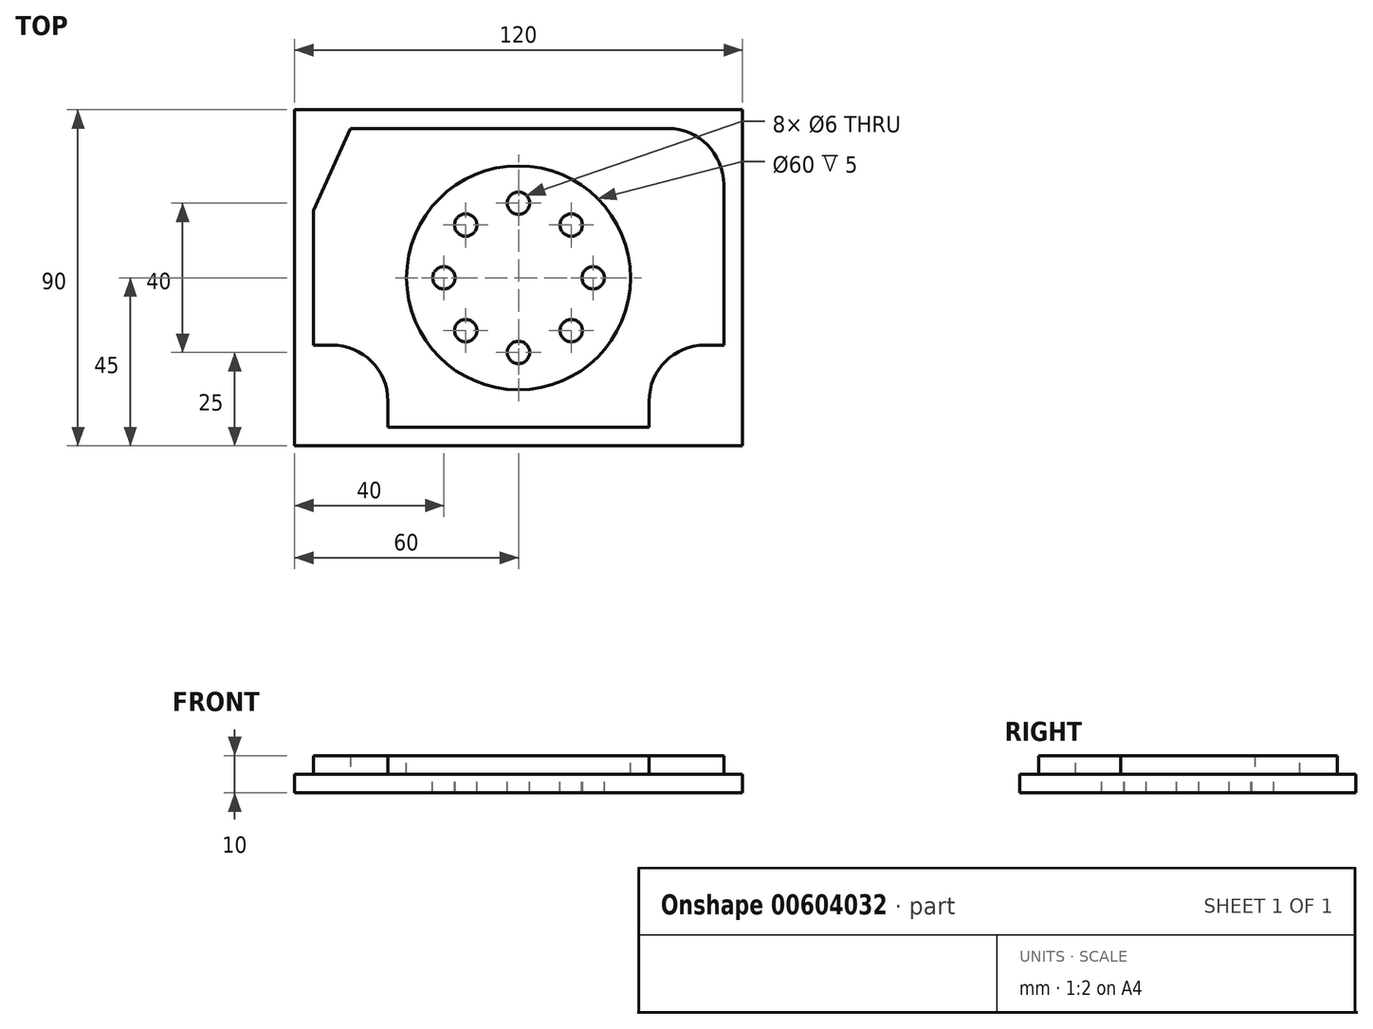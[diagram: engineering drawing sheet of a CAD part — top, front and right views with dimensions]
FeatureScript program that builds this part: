
annotation { "Feature Type Name" : "Feature", "Feature Type Description" : "" }
export const myFeature = defineFeature(function(context is Context, id is Id, definition is map)
    precondition{}
    {
        {
            var Q0;
            Q0=qCreatedBy(makeId("Top.planeOp"),FACE);
            var sketch = newSketch(context, id + "F0", { "sketchPlane" : qUnion([Q0])});
            skLineSegment(sketch, "E0.bottom", {"start": v(0, 0) * mm, "end": v(-120, 0) * mm});
            skLineSegment(sketch, "E0.top", {"start": v(0, 90) * mm, "end": v(-120, 90) * mm});
            skLineSegment(sketch, "E0.left", {"start": v(0, 0) * mm, "end": v(0, 90) * mm});
            skLineSegment(sketch, "E0.right", {"start": v(-120, 0) * mm, "end": v(-120, 90) * mm});
            skSolve(sketch);
        }
        {
            var Q0;
            Q0 = qSketchRegion(id + "F0", true);
            extrude(context, id + "F1", {"entities" : qUnion([Q0]), "depth" : 5 * mm, "offsetDistance" : 25 * mm});
        }
        {
            var Q0;
            Q0=makeQuery(id+"F1.opExtrude","CAP_FACE",FACE,{"disambiguationData":[OSD([sQuery(id+"F0.wireOp",EDGE,"E0.bottom"),sQuery(id+"F0.wireOp",EDGE,"E0.top"),sQuery(id+"F0.wireOp",EDGE,"E0.left"),sQuery(id+"F0.wireOp",EDGE,"E0.right")])],"isStart":false});
            var sketch = newSketch(context, id + "F2", { "sketchPlane" : qUnion([Q0])});
            skLineSegment(sketch, "E1", {"start": v(0, 0) * mm, "end": v(-5, 0) * mm, "construction": true});
            skLineSegment(sketch, "E2", {"start": v(-5, 0) * mm, "end": v(-5, 27) * mm, "construction": true});
            skLineSegment(sketch, "E3", {"start": v(-5, 27) * mm, "end": v(-5, 70) * mm});
            skLineSegment(sketch, "E4", {"start": v(-20, 85) * mm, "end": v(-105, 85) * mm});
            skPoint(sketch, "E5.visualSharp", {"position": v(-5, 85) * mm});
            skArc(sketch, "E5.filletArc", {"start": v(-5, 70) * mm, "mid": v(-9.4, 80.6) * mm, "end": v(-20, 85) * mm});
            skLineSegment(sketch, "E6", {"start": v(-5, 27) * mm, "end": v(-10, 27) * mm});
            skLineSegment(sketch, "E7", {"start": v(-25, 12) * mm, "end": v(-25, 5) * mm});
            skPoint(sketch, "E8.visualSharp", {"position": v(-25, 27) * mm});
            skArc(sketch, "E8.filletArc", {"start": v(-10, 27) * mm, "mid": v(-20.6, 22.6) * mm, "end": v(-25, 12) * mm});
            skLineSegment(sketch, "E9", {"start": v(-25, 5) * mm, "end": v(-95, 5) * mm});
            skLineSegment(sketch, "E10", {"start": v(-95, 5) * mm, "end": v(-95, 12) * mm});
            skLineSegment(sketch, "E11", {"start": v(-110, 27) * mm, "end": v(-115, 27) * mm});
            skPoint(sketch, "E12.visualSharp", {"position": v(-95, 27) * mm});
            skArc(sketch, "E12.filletArc", {"start": v(-95, 12) * mm, "mid": v(-99.4, 22.6) * mm, "end": v(-110, 27) * mm});
            skLineSegment(sketch, "E13", {"start": v(-115, 27) * mm, "end": v(-115, 63) * mm});
            skLineSegment(sketch, "E14", {"start": v(-115, 63) * mm, "end": v(-105, 85) * mm});
            skSolve(sketch);
        }
        {
            var Q0;
            Q0 = qSketchRegion(id + "F2", true);
            extrude(context, id + "F3", {"entities" : qUnion([Q0]), "operationType" : NewBodyOperationType.ADD, "depth" : 5 * mm, "offsetDistance" : 25 * mm});
        }
        {
            var Q0;
            Q0=makeQuery(id+"F3.opExtrude","CAP_FACE",FACE,{"disambiguationData":[OSD([sQuery(id+"F2.wireOp",EDGE,"E3"),sQuery(id+"F2.wireOp",EDGE,"E4"),sQuery(id+"F2.wireOp",EDGE,"E5.filletArc"),sQuery(id+"F2.wireOp",EDGE,"E6"),sQuery(id+"F2.wireOp",EDGE,"E7"),sQuery(id+"F2.wireOp",EDGE,"E8.filletArc"),sQuery(id+"F2.wireOp",EDGE,"E9"),sQuery(id+"F2.wireOp",EDGE,"E10"),sQuery(id+"F2.wireOp",EDGE,"E11"),sQuery(id+"F2.wireOp",EDGE,"E12.filletArc"),sQuery(id+"F2.wireOp",EDGE,"E13"),sQuery(id+"F2.wireOp",EDGE,"E14")])],"isStart":false});
            var sketch = newSketch(context, id + "F4", { "sketchPlane" : qUnion([Q0])});
            skCircle(sketch, "E15", {"center": v(-60, 45) * mm, "radius": 30 * mm});
            skSolve(sketch);
        }
        {
            var Q0;
            Q0 = qSketchRegion(id + "F4", true);
            extrude(context, id + "F5", {"entities" : qUnion([Q0]), "operationType" : NewBodyOperationType.REMOVE, "oppositeDirection" : true, "depth" : 5 * mm, "offsetDistance" : 25 * mm});
        }
        {
            var Q0;
            Q0=makeQuery(id+"F3.opExtrude","CAP_FACE",FACE,{"disambiguationData":[OSD([sQuery(id+"F2.wireOp",EDGE,"E3"),sQuery(id+"F2.wireOp",EDGE,"E4"),sQuery(id+"F2.wireOp",EDGE,"E5.filletArc"),sQuery(id+"F2.wireOp",EDGE,"E6"),sQuery(id+"F2.wireOp",EDGE,"E7"),sQuery(id+"F2.wireOp",EDGE,"E8.filletArc"),sQuery(id+"F2.wireOp",EDGE,"E9"),sQuery(id+"F2.wireOp",EDGE,"E10"),sQuery(id+"F2.wireOp",EDGE,"E11"),sQuery(id+"F2.wireOp",EDGE,"E12.filletArc"),sQuery(id+"F2.wireOp",EDGE,"E13"),sQuery(id+"F2.wireOp",EDGE,"E14")])],"isStart":false});
            var sketch = newSketch(context, id + "F6", { "sketchPlane" : qUnion([Q0])});
            skCircle(sketch, "E16", {"center": v(-60, 45) * mm, "radius": 20 * mm, "construction": true});
            skCircle(sketch, "E17", {"center": v(-80, 45) * mm, "radius": 3 * mm});
            skCircle(sketch, "E18", {"center": v(-60, 25) * mm, "radius": 3 * mm});
            skCircle(sketch, "E19", {"center": v(-60, 65) * mm, "radius": 3 * mm});
            skCircle(sketch, "E20", {"center": v(-40, 45) * mm, "radius": 3 * mm});
            skCircle(sketch, "E21", {"center": v(-74.14, 59.14) * mm, "radius": 3 * mm});
            skCircle(sketch, "E22", {"center": v(-45.86, 59.14) * mm, "radius": 3 * mm});
            skCircle(sketch, "E23", {"center": v(-74.14, 30.86) * mm, "radius": 3 * mm});
            skCircle(sketch, "E24", {"center": v(-45.86, 30.86) * mm, "radius": 3 * mm});
            skSolve(sketch);
        }
        {
            var Q0;
            Q0 = qSketchRegion(id + "F6", true);
            extrude(context, id + "F7", {"entities" : qUnion([Q0]), "operationType" : NewBodyOperationType.REMOVE, "oppositeDirection" : true, "depth" : 25 * mm, "offsetDistance" : 25 * mm});
        }
    });
